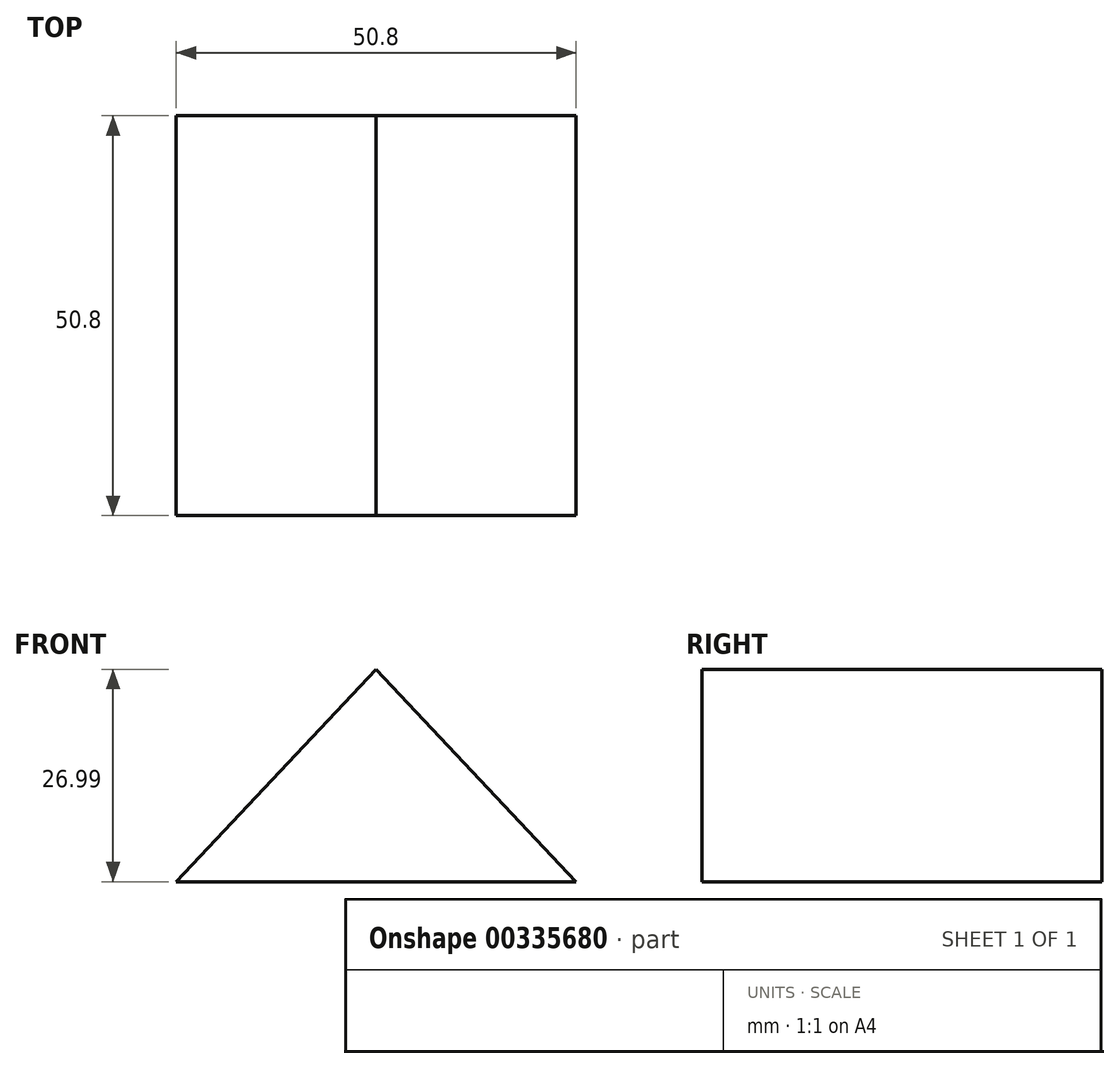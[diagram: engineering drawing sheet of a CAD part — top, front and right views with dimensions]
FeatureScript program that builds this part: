
annotation { "Feature Type Name" : "Feature", "Feature Type Description" : "" }
export const myFeature = defineFeature(function(context is Context, id is Id, definition is map)
    precondition{}
    {
        {
            var Q0;
            Q0=qCreatedBy(makeId("Front.planeOp"),FACE);
            var sketch = newSketch(context, id + "F0", { "sketchPlane" : qUnion([Q0])});
            skLineSegment(sketch, "E0", {"start": v(0, 0) * mm, "end": v(25.4, 0) * mm});
            skLineSegment(sketch, "E1", {"start": v(25.4, 0) * mm, "end": v(0, 0) * mm});
            skLineSegment(sketch, "E2", {"start": v(0, 0) * mm, "end": v(-25.4, 0) * mm});
            skLineSegment(sketch, "E3", {"start": v(-25.4, 0) * mm, "end": v(0, 0) * mm});
            skLineSegment(sketch, "E4", {"start": v(0, 0) * mm, "end": v(0, 27) * mm});
            skLineSegment(sketch, "E5", {"start": v(-25.4, 0) * mm, "end": v(0, 27) * mm});
            skLineSegment(sketch, "E6", {"start": v(25.4, 0) * mm, "end": v(0, 27) * mm});
            skSolve(sketch);
        }
        {
            var Q0;
            Q0 = qSketchRegion(id + "F0", true);
            extrude(context, id + "F1", {"entities" : qUnion([Q0]), "depth" : 50.8 * mm});
        }
    });
